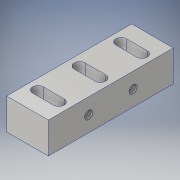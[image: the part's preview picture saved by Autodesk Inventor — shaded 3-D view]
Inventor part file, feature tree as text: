
AUTODESK INVENTOR PART (.ipt)
format: ipt  version: 2016 (Build 200138000, 138)  size: 138,752 bytes
history: native  units: in
note: dims shown in document units (in); Inventor stores cm internally (conversion verified against a paired STEP export)
features: sketch x3, extrude x2, hole x1
ambient origin geometry x8: Origin, YZ Plane, XZ Plane, XY Plane, X Axis, Y Axis, Z Axis, Center Point
bodies: Solid1 (feature_tree)
feature tree (6):
  extrude  "Extrusion1"  Depth=0.75in
  hole  "Hole1"  [1 undecoded]
  extrude  "Extrusion2"  Depth=1.0in
  sketch  "Sketch1"  dims[d0=1.0in d1=0.75in]
  sketch  "Sketch2"  dims[d2=3.0in d3=0.0in d4=1.068in]
  sketch  "Sketch3"  dims[d6=0.375in d7=0.375in d8=0.196in d9=0.875in d10=0.375in d11=0.25in d12=0.5635in d13=0.875in d14=0.8108in d15=0.13in d16=0.13in d17=0.13in d18=0.5in d19=0.5in d20=0.5in d21=1.0in d22=1.0in d23=0.25in d24=0.25in d25=0.25in d26=0.5in d27=4.0in d28=0.0in d29=0.966in]
note: 1 required parameter value undecoded (feature->parameter linkage not recoverable at this tier; creation-order binding heuristic only, values carry confidence <= 0.55)
